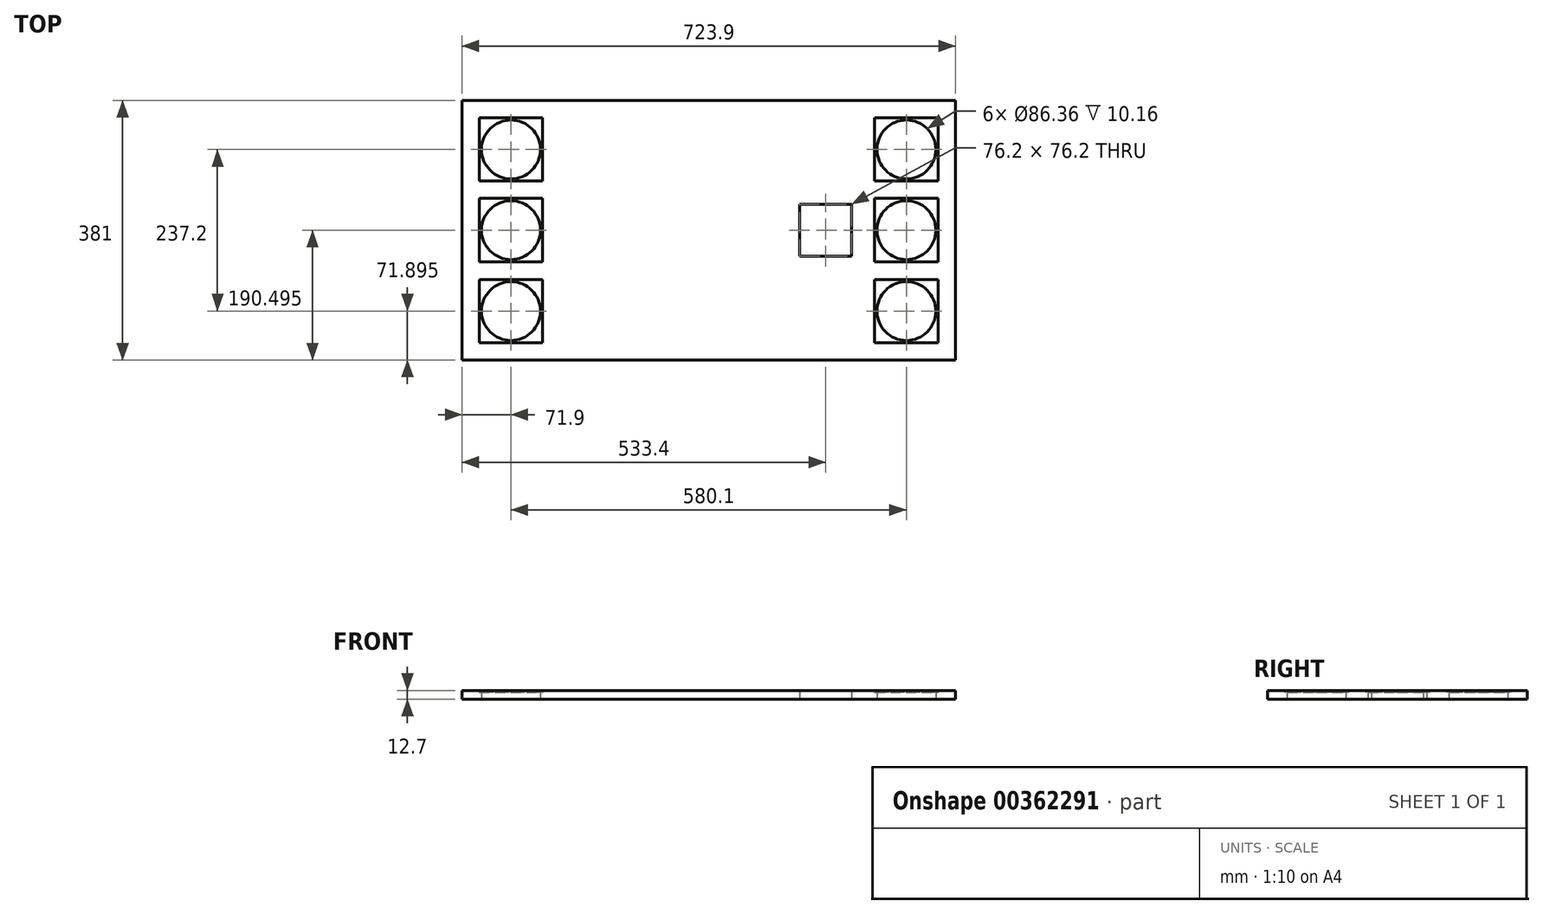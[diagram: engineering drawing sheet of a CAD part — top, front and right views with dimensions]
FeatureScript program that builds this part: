
annotation { "Feature Type Name" : "Feature", "Feature Type Description" : "" }
export const myFeature = defineFeature(function(context is Context, id is Id, definition is map)
    precondition{}
    {
        {
            var Q0;
            Q0=qCreatedBy(makeId("Top.planeOp"),FACE);
            var sketch = newSketch(context, id + "F0", { "sketchPlane" : qUnion([Q0])});
            skLineSegment(sketch, "E0.bottom", {"start": v(-373.63, 227.64) * mm, "end": v(350.27, 227.64) * mm});
            skLineSegment(sketch, "E0.top", {"start": v(-373.63, -153.36) * mm, "end": v(350.27, -153.36) * mm});
            skLineSegment(sketch, "E0.left", {"start": v(-373.63, 227.64) * mm, "end": v(-373.63, -153.36) * mm});
            skLineSegment(sketch, "E0.right", {"start": v(350.27, 227.64) * mm, "end": v(350.27, -153.36) * mm});
            skLineSegment(sketch, "E1.bottom", {"start": v(121.67, 75.24) * mm, "end": v(197.87, 75.24) * mm});
            skLineSegment(sketch, "E1.top", {"start": v(121.67, -0.96) * mm, "end": v(197.87, -0.96) * mm});
            skLineSegment(sketch, "E1.left", {"start": v(121.67, 75.24) * mm, "end": v(121.67, -0.96) * mm});
            skLineSegment(sketch, "E1.right", {"start": v(197.87, 75.24) * mm, "end": v(197.87, -0.96) * mm});
            skLineSegment(sketch, "E2.bottom", {"start": v(231.87, -34.96) * mm, "end": v(324.87, -34.96) * mm});
            skLineSegment(sketch, "E2.top", {"start": v(231.87, -127.96) * mm, "end": v(324.87, -127.96) * mm});
            skLineSegment(sketch, "E2.left", {"start": v(231.87, -34.96) * mm, "end": v(231.87, -127.96) * mm});
            skLineSegment(sketch, "E2.right", {"start": v(324.87, -34.96) * mm, "end": v(324.87, -127.96) * mm});
            skLineSegment(sketch, "E3.bottom", {"start": v(231.87, 202.24) * mm, "end": v(324.87, 202.24) * mm});
            skLineSegment(sketch, "E3.top", {"start": v(231.87, 109.24) * mm, "end": v(324.87, 109.24) * mm});
            skLineSegment(sketch, "E3.left", {"start": v(231.87, 202.24) * mm, "end": v(231.87, 109.24) * mm});
            skLineSegment(sketch, "E3.right", {"start": v(324.87, 202.24) * mm, "end": v(324.87, 109.24) * mm});
            skLineSegment(sketch, "E4.bottom", {"start": v(231.87, 83.84) * mm, "end": v(324.87, 83.84) * mm});
            skLineSegment(sketch, "E4.top", {"start": v(231.87, -9.16) * mm, "end": v(324.87, -9.16) * mm});
            skLineSegment(sketch, "E4.left", {"start": v(231.87, 83.84) * mm, "end": v(231.87, -9.16) * mm});
            skLineSegment(sketch, "E4.right", {"start": v(324.87, 83.84) * mm, "end": v(324.87, -9.16) * mm});
            skCircle(sketch, "E5", {"center": v(278.37, 155.74) * mm, "radius": 43.18 * mm});
            skPoint(sketch, "E5.centerSnap0", {"position": v(278.37, 202.24) * mm});
            skPoint(sketch, "E5.centerSnap1", {"position": v(231.87, 155.74) * mm});
            skCircle(sketch, "E6", {"center": v(278.37, 37.34) * mm, "radius": 43.18 * mm});
            skPoint(sketch, "E6.centerSnap0", {"position": v(231.87, 37.34) * mm});
            skPoint(sketch, "E6.centerSnap1", {"position": v(278.37, 83.84) * mm});
            skCircle(sketch, "E7", {"center": v(278.37, -81.46) * mm, "radius": 43.18 * mm});
            skPoint(sketch, "E7.centerSnap0", {"position": v(231.87, -81.46) * mm});
            skPoint(sketch, "E7.centerSnap1", {"position": v(278.37, -34.96) * mm});
            skLineSegment(sketch, "E8.bottom", {"start": v(-348.23, -34.96) * mm, "end": v(-255.23, -34.96) * mm});
            skLineSegment(sketch, "E8.top", {"start": v(-348.23, -127.96) * mm, "end": v(-255.23, -127.96) * mm});
            skLineSegment(sketch, "E8.left", {"start": v(-348.23, -34.96) * mm, "end": v(-348.23, -127.96) * mm});
            skLineSegment(sketch, "E8.right", {"start": v(-255.23, -34.96) * mm, "end": v(-255.23, -127.96) * mm});
            skLineSegment(sketch, "E9.bottom", {"start": v(-348.23, 202.24) * mm, "end": v(-255.23, 202.24) * mm});
            skLineSegment(sketch, "E9.top", {"start": v(-348.23, 109.24) * mm, "end": v(-255.23, 109.24) * mm});
            skLineSegment(sketch, "E9.left", {"start": v(-348.23, 202.24) * mm, "end": v(-348.23, 109.24) * mm});
            skLineSegment(sketch, "E9.right", {"start": v(-255.23, 202.24) * mm, "end": v(-255.23, 109.24) * mm});
            skLineSegment(sketch, "E10.bottom", {"start": v(-348.23, 83.84) * mm, "end": v(-255.23, 83.84) * mm});
            skLineSegment(sketch, "E10.top", {"start": v(-348.23, -9.16) * mm, "end": v(-255.23, -9.16) * mm});
            skLineSegment(sketch, "E10.left", {"start": v(-348.23, 83.84) * mm, "end": v(-348.23, -9.16) * mm});
            skLineSegment(sketch, "E10.right", {"start": v(-255.23, 83.84) * mm, "end": v(-255.23, -9.16) * mm});
            skCircle(sketch, "E11", {"center": v(-301.73, 155.74) * mm, "radius": 43.18 * mm});
            skPoint(sketch, "E11.centerSnap0", {"position": v(-301.73, 202.24) * mm});
            skPoint(sketch, "E11.centerSnap1", {"position": v(-348.23, 155.74) * mm});
            skCircle(sketch, "E12", {"center": v(-301.73, 37.34) * mm, "radius": 43.18 * mm});
            skPoint(sketch, "E12.centerSnap0", {"position": v(-348.23, 37.34) * mm});
            skPoint(sketch, "E12.centerSnap1", {"position": v(-301.73, 83.84) * mm});
            skCircle(sketch, "E13", {"center": v(-301.73, -81.46) * mm, "radius": 43.18 * mm});
            skPoint(sketch, "E13.centerSnap0", {"position": v(-348.23, -81.46) * mm});
            skPoint(sketch, "E13.centerSnap1", {"position": v(-301.73, -34.96) * mm});
            skSolve(sketch);
        }
        {
            var Q0;
            Q0 = qSketchRegion(id + "F0", true);
            extrude(context, id + "F1", {"entities" : qUnion([Q0]), "depth" : 12.7 * mm});
        }
        {
            var Q0;
            Q0=makeQuery(id+"F0.imprint","IMPRINT",FACE,{"disambiguationData":[TD([[makeQuery(id+"F0.imprint","IMPRINT",EDGE,{"derivedFrom":sQuery(id+"F0.wireOp",EDGE,"E3.bottom")}),-1.0]])]});
            var Q1;
            Q1=makeQuery(id+"F0.imprint","IMPRINT",FACE,{"disambiguationData":[TD([[makeQuery(id+"F0.imprint","IMPRINT",EDGE,{"derivedFrom":sQuery(id+"F0.wireOp",EDGE,"E4.bottom")}),-1.0]])]});
            var Q2;
            Q2=makeQuery(id+"F0.imprint","IMPRINT",FACE,{"disambiguationData":[TD([[makeQuery(id+"F0.imprint","IMPRINT",EDGE,{"derivedFrom":sQuery(id+"F0.wireOp",EDGE,"E2.bottom")}),-1.0]])]});
            extrude(context, id + "F2", {"entities" : qUnion([Q0, Q1, Q2]), "operationType" : NewBodyOperationType.ADD, "depth" : 10.16 * mm});
        }
        {
            var Q0;
            Q0=makeQuery(id+"F0.imprint","IMPRINT",FACE,{"disambiguationData":[TD([[makeQuery(id+"F0.imprint","IMPRINT",EDGE,{"derivedFrom":sQuery(id+"F0.wireOp",EDGE,"E5")}),1.0]])]});
            var Q1;
            Q1=makeQuery(id+"F0.imprint","IMPRINT",FACE,{"disambiguationData":[TD([[makeQuery(id+"F0.imprint","IMPRINT",EDGE,{"derivedFrom":sQuery(id+"F0.wireOp",EDGE,"E6")}),1.0]])]});
            var Q2;
            Q2=makeQuery(id+"F0.imprint","IMPRINT",FACE,{"disambiguationData":[TD([[makeQuery(id+"F0.imprint","IMPRINT",EDGE,{"derivedFrom":sQuery(id+"F0.wireOp",EDGE,"E7")}),1.0]])]});
            extrude(context, id + "F3", {"entities" : qUnion([Q0, Q1, Q2]), "operationType" : NewBodyOperationType.REMOVE, "depth" : 25.4 * mm});
        }
        {
            var Q0;
            Q0=makeQuery(id+"F0.imprint","IMPRINT",FACE,{"disambiguationData":[TD([[makeQuery(id+"F0.imprint","IMPRINT",EDGE,{"derivedFrom":sQuery(id+"F0.wireOp",EDGE,"E9.bottom")}),-1.0]])]});
            var Q1;
            Q1=makeQuery(id+"F0.imprint","IMPRINT",FACE,{"disambiguationData":[TD([[makeQuery(id+"F0.imprint","IMPRINT",EDGE,{"derivedFrom":sQuery(id+"F0.wireOp",EDGE,"E10.bottom")}),-1.0]])]});
            var Q2;
            Q2=makeQuery(id+"F0.imprint","IMPRINT",FACE,{"disambiguationData":[TD([[makeQuery(id+"F0.imprint","IMPRINT",EDGE,{"derivedFrom":sQuery(id+"F0.wireOp",EDGE,"E8.bottom")}),-1.0]])]});
            extrude(context, id + "F4", {"entities" : qUnion([Q0, Q1, Q2]), "operationType" : NewBodyOperationType.ADD, "depth" : 10.16 * mm});
        }
    });
